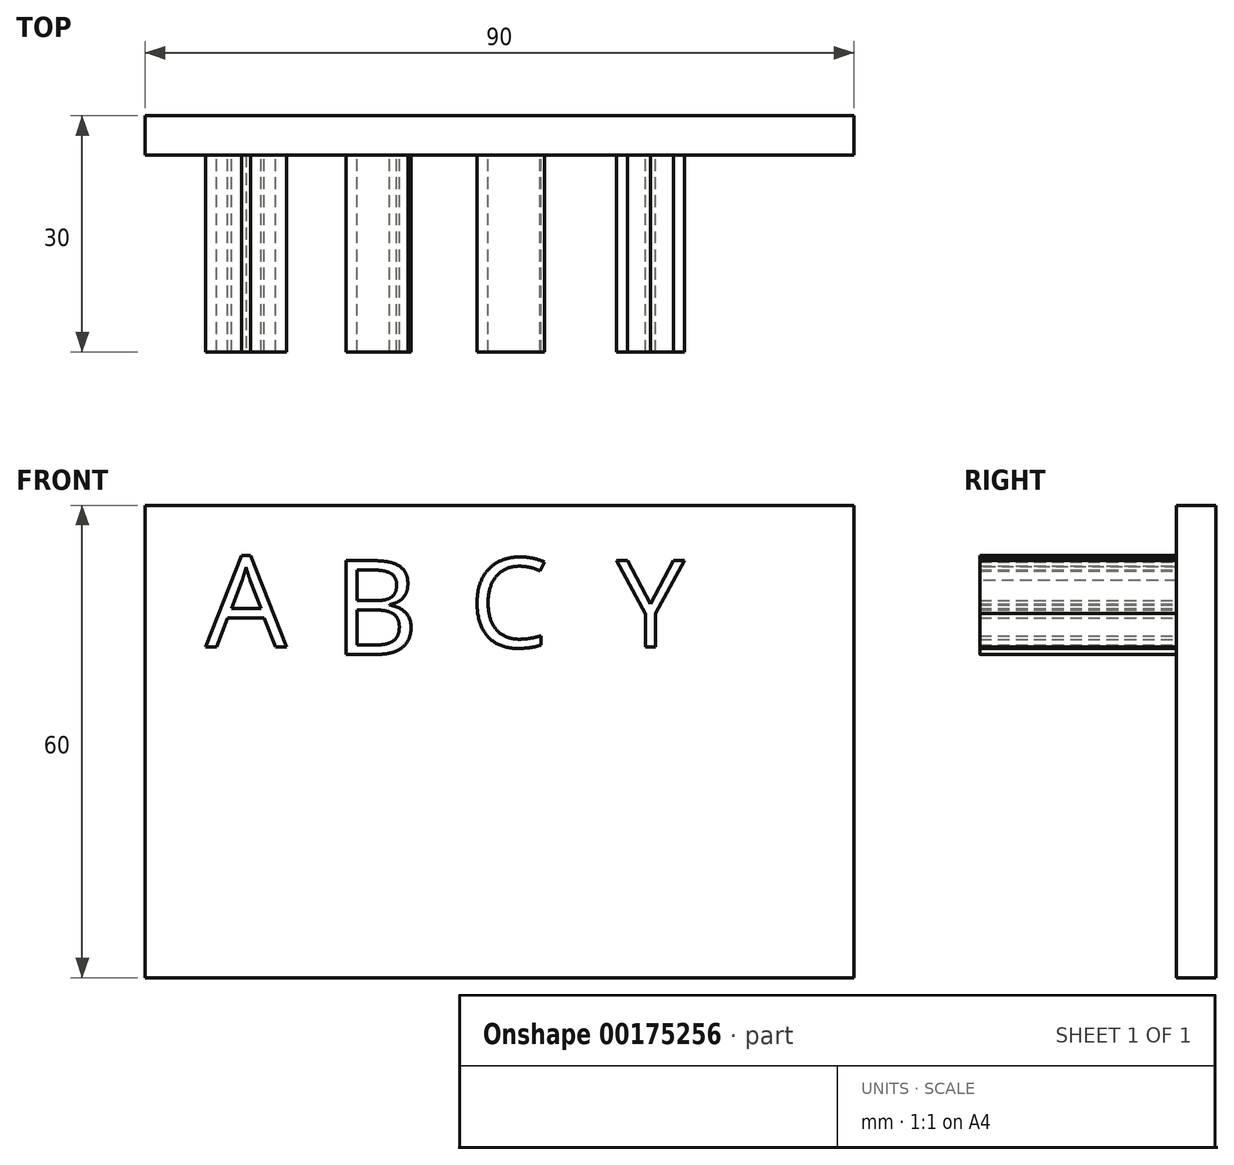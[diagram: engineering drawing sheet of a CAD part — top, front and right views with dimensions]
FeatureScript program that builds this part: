
annotation { "Feature Type Name" : "Feature", "Feature Type Description" : "" }
export const myFeature = defineFeature(function(context is Context, id is Id, definition is map)
    precondition{}
    {
        {
            var Q0;
            Q0=qCreatedBy(makeId("Front.planeOp"),FACE);
            var sketch = newSketch(context, id + "F0", { "sketchPlane" : qUnion([Q0])});
            skLineSegment(sketch, "E0.bottom", {"start": v(-41.18, 33.63) * mm, "end": v(48.82, 33.63) * mm});
            skLineSegment(sketch, "E0.top", {"start": v(-41.18, -26.37) * mm, "end": v(48.82, -26.37) * mm});
            skLineSegment(sketch, "E0.left", {"start": v(-41.18, 33.63) * mm, "end": v(-41.18, -26.37) * mm});
            skLineSegment(sketch, "E0.right", {"start": v(48.82, 33.63) * mm, "end": v(48.82, -26.37) * mm});
            skSolve(sketch);
        }
        {
            var Q0;
            Q0=makeQuery(id+"F0.imprint","IMPRINT",FACE,{"disambiguationData":[TD([[makeQuery(id+"F0.imprint","IMPRINT",EDGE,{"derivedFrom":sQuery(id+"F0.wireOp",EDGE,"E0.bottom")}),-1.0]])]});
            extrude(context, id + "F1", {"entities" : qUnion([Q0]), "depth" : 5 * mm});
        }
        {
            var Q0;
            Q0=makeQuery(id+"F1.opExtrude","CAP_FACE",FACE,{"disambiguationData":[OSD([sQuery(id+"F0.wireOp",EDGE,"E0.bottom"),sQuery(id+"F0.wireOp",EDGE,"E0.top"),sQuery(id+"F0.wireOp",EDGE,"E0.left"),sQuery(id+"F0.wireOp",EDGE,"E0.right")])],"isStart":false});
            var sketch = newSketch(context, id + "F2", { "sketchPlane" : qUnion([Q0])});
            skText(sketch, "E1", { "text": "A", "fontName": "OpenSans-Regular.ttf"});
            skText(sketch, "E2", { "text": "B", "fontName": "OpenSans-Regular.ttf"});
            skText(sketch, "E3", { "text": "C", "fontName": "OpenSans-Regular.ttf"});
            skText(sketch, "E4", { "text": "Y\n", "fontName": "OpenSans-Regular.ttf"});
            const initialGuessF2  = {"E1": [-0.03351, 0.01562, 1, 0, 0.0117], "E2": [-0.0173, 0.01472, 1, 0, 0.012], "E3": [0, 0.01562, 1, 0, 0.0114], "E4": [0.0187, 0.01562, 1, 0, 0.0111]};
            skSetInitialGuess(sketch, initialGuessF2);
            skSolve(sketch);
        }
        {
            var Q0;
            Q0 = qSketchRegion(id + "F2", true);
            extrude(context, id + "F3", {"entities" : qUnion([Q0]), "operationType" : NewBodyOperationType.ADD, "depth" : 25 * mm});
        }
    });
